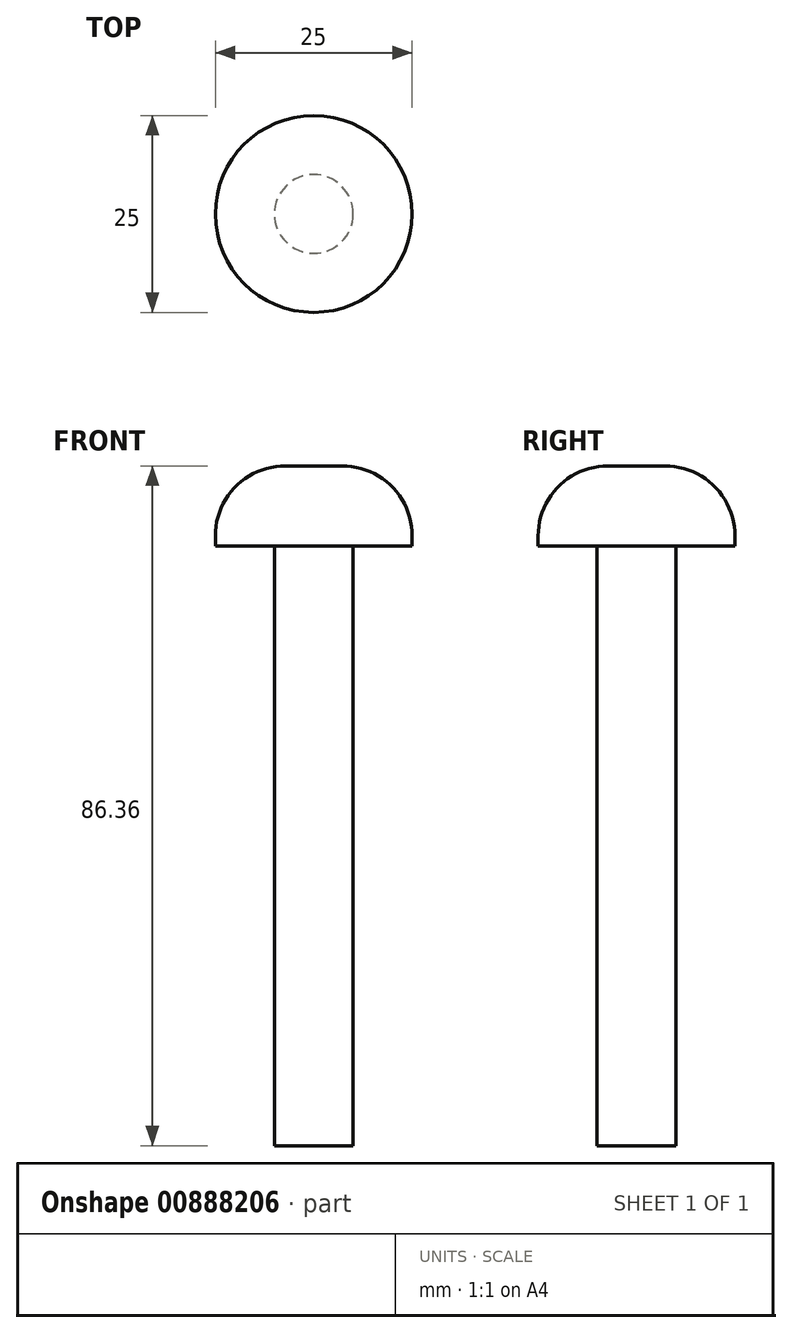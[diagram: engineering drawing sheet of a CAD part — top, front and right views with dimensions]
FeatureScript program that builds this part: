
annotation { "Feature Type Name" : "Feature", "Feature Type Description" : "" }
export const myFeature = defineFeature(function(context is Context, id is Id, definition is map)
    precondition{}
    {
        {
            var Q0;
            Q0=qCreatedBy(makeId("Top.planeOp"),FACE);
            var sketch = newSketch(context, id + "F0", { "sketchPlane" : qUnion([Q0])});
            skCircle(sketch, "E0", {"center": v(0, 0) * mm, "radius": 5 * mm});
            skSolve(sketch);
        }
        {
            var Q0;
            Q0=makeQuery(id+"F0.imprint","IMPRINT",FACE,{"disambiguationData":[TD([[makeQuery(id+"F0.imprint","IMPRINT",EDGE,{"derivedFrom":sQuery(id+"F0.wireOp",EDGE,"E0")}),1.0]])]});
            extrude(context, id + "F1", {"entities" : qUnion([Q0]), "depth" : 76.2 * mm, "offsetDistance" : 25.4 * mm});
        }
        {
            var Q0;
            Q0=makeQuery(id+"F1.opExtrude","CAP_FACE",FACE,{"disambiguationData":[OSD([sQuery(id+"F0.wireOp",EDGE,"E0")])],"isStart":false});
            var sketch = newSketch(context, id + "F2", { "sketchPlane" : qUnion([Q0])});
            skCircle(sketch, "E1", {"center": v(0, 0) * mm, "radius": 12.5 * mm});
            skSolve(sketch);
        }
        {
            var Q0;
            Q0=makeQuery(id+"F2.imprint","IMPRINT",FACE,{"disambiguationData":[TD([[makeQuery(id+"F2.imprint","IMPRINT",EDGE,{"derivedFrom":makeQuery(id+"F1.opExtrude","CAP_EDGE",EDGE,{"disambiguationData":[OSD([sQuery(id+"F0.wireOp",EDGE,"E0")])],"isStart":false})}),1.0]])]});
            var Q1;
            Q1=makeQuery(id+"F2.imprint","IMPRINT",FACE,{"disambiguationData":[TD([[makeQuery(id+"F2.imprint","IMPRINT",EDGE,{"derivedFrom":sQuery(id+"F2.wireOp",EDGE,"E1")}),1.0]])]});
            extrude(context, id + "F3", {"entities" : qUnion([Q0, Q1]), "operationType" : NewBodyOperationType.ADD, "depth" : 10.16 * mm, "offsetDistance" : 25.4 * mm});
        }
        {
            var Q0;
            Q0=makeQuery(id+"F3.opExtrude","CAP_FACE",FACE,{"disambiguationData":[OSD([sQuery(id+"F2.wireOp",EDGE,"E1")])],"isStart":false});
            fillet(context, id + "F4", {"entities" : qUnion([Q0]), "radius" : 8.9 * mm, "tangentPropagation" : true, "allowEdgeOverflow" : false});
        }
    });
